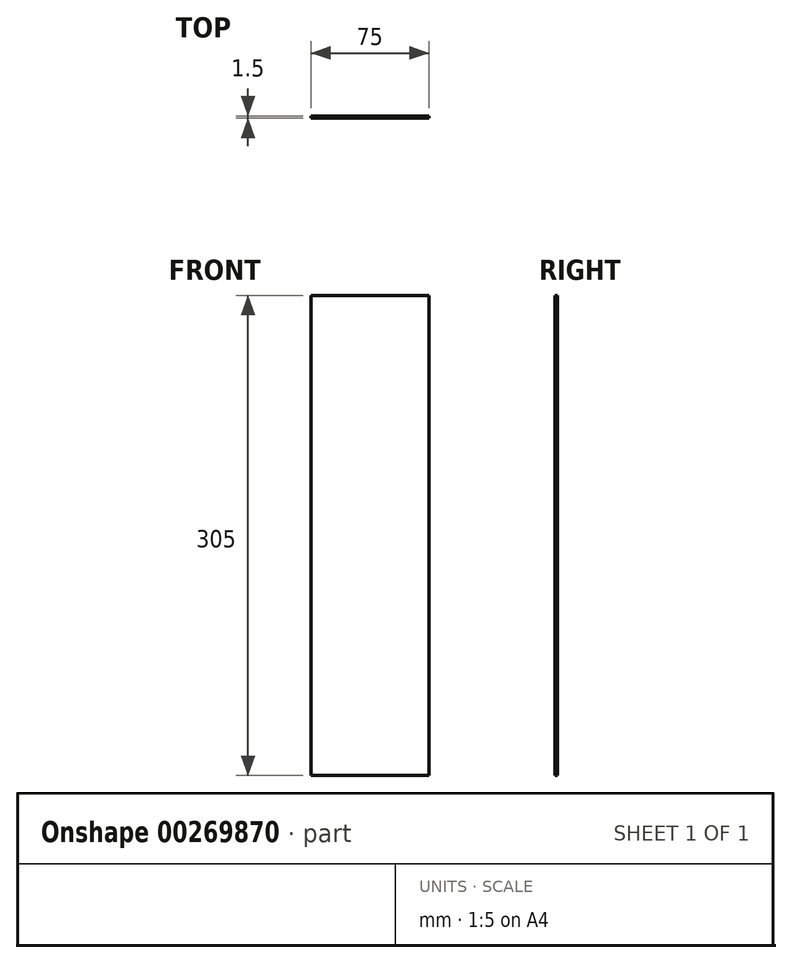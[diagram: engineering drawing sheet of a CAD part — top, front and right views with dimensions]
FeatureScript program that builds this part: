
annotation { "Feature Type Name" : "Feature", "Feature Type Description" : "" }
export const myFeature = defineFeature(function(context is Context, id is Id, definition is map)
    precondition{}
    {
        {
            var Q0;
            Q0=qCreatedBy(makeId("Front.planeOp"),FACE);
            var sketch = newSketch(context, id + "F0", { "sketchPlane" : qUnion([Q0])});
            skLineSegment(sketch, "E0.bottom", {"start": v(0, 0) * mm, "end": v(75, 0) * mm});
            skLineSegment(sketch, "E0.top", {"start": v(0, 305) * mm, "end": v(75, 305) * mm});
            skLineSegment(sketch, "E0.left", {"start": v(0, 0) * mm, "end": v(0, 305) * mm});
            skLineSegment(sketch, "E0.right", {"start": v(75, 0) * mm, "end": v(75, 305) * mm});
            skSolve(sketch);
        }
        {
            var Q0;
            Q0 = qSketchRegion(id + "F0", true);
            extrude(context, id + "F1", {"entities" : qUnion([Q0]), "offsetDistance" : 25.4 * mm, "depth" : 1.5 * mm});
        }
    });
